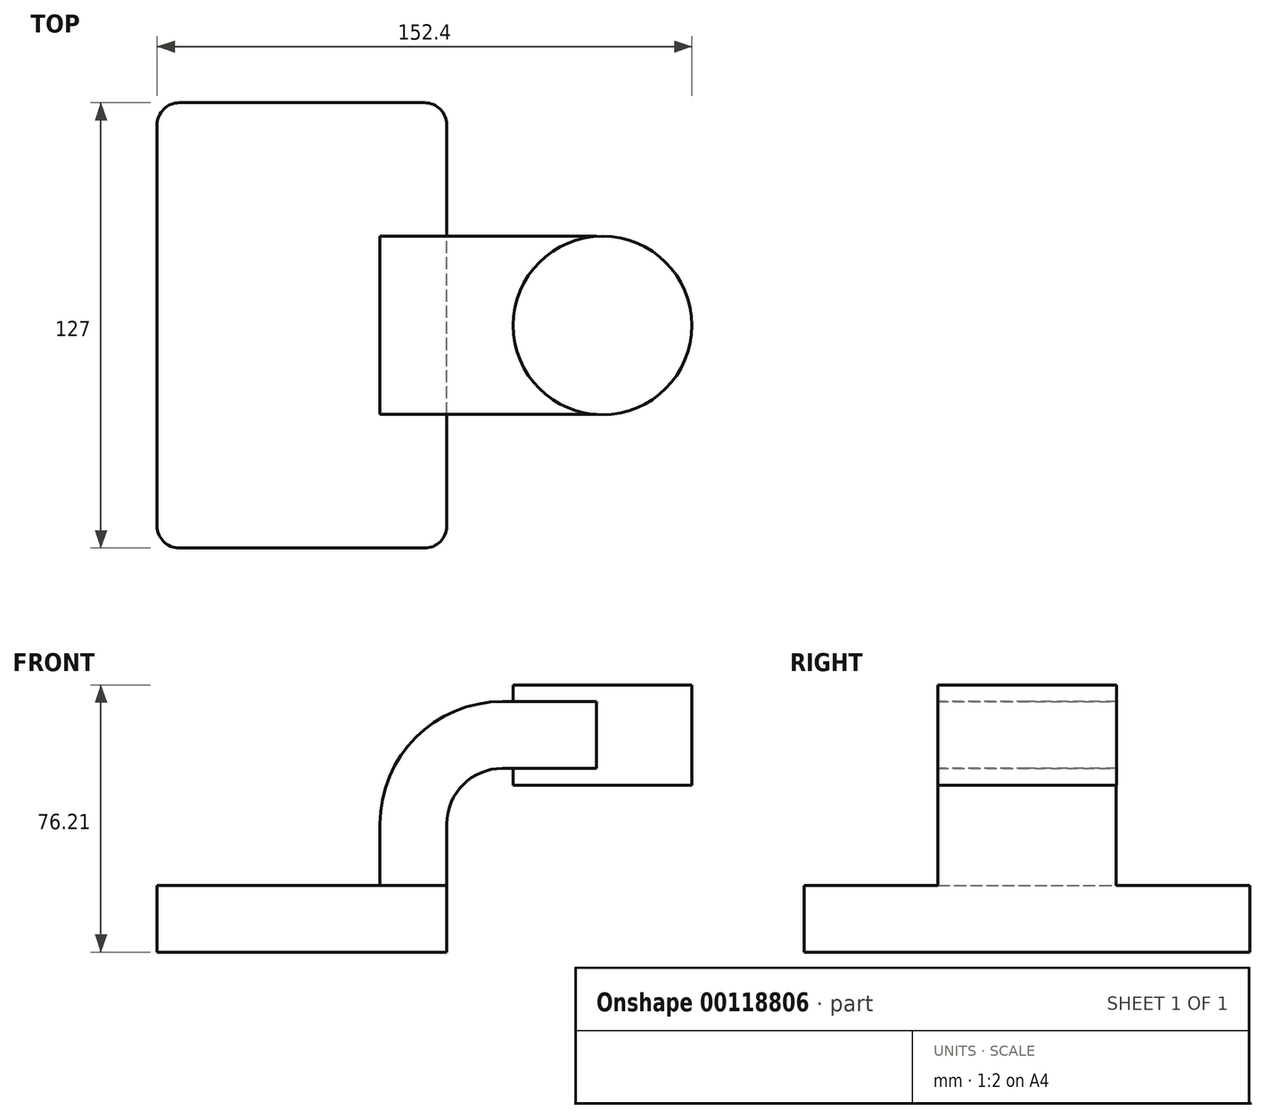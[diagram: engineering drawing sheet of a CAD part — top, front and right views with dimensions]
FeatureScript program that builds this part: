
annotation { "Feature Type Name" : "Feature", "Feature Type Description" : "" }
export const myFeature = defineFeature(function(context is Context, id is Id, definition is map)
    precondition{}
    {
        {
            var Q0;
            Q0=qCreatedBy(makeId("Front.planeOp"),FACE);
            var sketch = newSketch(context, id + "F0", { "sketchPlane" : qUnion([Q0])});
            skLineSegment(sketch, "E0.bottom", {"start": v(-41.28, -9.53) * mm, "end": v(41.28, -9.53) * mm});
            skLineSegment(sketch, "E0.top", {"start": v(-41.28, 9.53) * mm, "end": v(41.28, 9.53) * mm});
            skLineSegment(sketch, "E0.left", {"start": v(-41.28, -9.53) * mm, "end": v(-41.28, 9.53) * mm});
            skLineSegment(sketch, "E0.right", {"start": v(41.28, -9.53) * mm, "end": v(41.28, 9.53) * mm});
            skPoint(sketch, "E0.middle", {"position": v(0, 0) * mm});
            skLineSegment(sketch, "E1.bottom", {"start": v(60.32, 38.1) * mm, "end": v(111.12, 38.1) * mm});
            skLineSegment(sketch, "E1.top", {"start": v(60.32, 66.67) * mm, "end": v(111.12, 66.67) * mm});
            skLineSegment(sketch, "E1.left", {"start": v(60.32, 38.1) * mm, "end": v(60.32, 66.67) * mm});
            skLineSegment(sketch, "E1.right", {"start": v(111.12, 38.1) * mm, "end": v(111.12, 66.67) * mm});
            skPoint(sketch, "E1.middle", {"position": v(85.72, 52.39) * mm});
            skLineSegment(sketch, "E2", {"start": v(41.28, 9.53) * mm, "end": v(41.28, 27) * mm});
            skArc(sketch, "E3", {"start": v(41.27, 27) * mm, "mid": v(45.92, 38.23) * mm, "end": v(57.15, 42.88) * mm});
            skLineSegment(sketch, "E4", {"start": v(57.15, 42.88) * mm, "end": v(85.66, 42.88) * mm});
            skLineSegment(sketch, "E5.0", {"start": v(57.15, 61.93) * mm, "end": v(85.66, 61.93) * mm});
            skArc(sketch, "E5.1", {"start": v(22.22, 27) * mm, "mid": v(32.45, 51.7) * mm, "end": v(57.15, 61.93) * mm});
            skLineSegment(sketch, "E5.2", {"start": v(22.22, 9.53) * mm, "end": v(22.22, 27) * mm});
            skLineSegment(sketch, "E6", {"start": v(85.66, 38.1) * mm, "end": v(85.66, 66.67) * mm});
            skFitSpline(sketch, "E7", {"points": [v(-41.28, 9.53) * mm, v(57.15, 61.93) * mm], "startDerivative": vector(0.8, 87.71) * mm, "endDerivative": vector(119.82, -11.25) * mm});
            skSolve(sketch);
        }
        {
            var Q0;
            Q0=makeQuery(id+"F0.imprint","IMPRINT",FACE,{"disambiguationData":[TD([[makeQuery(id+"F0.imprint","IMPRINT",EDGE,{"derivedFrom":sQuery(id+"F0.wireOp",EDGE,"E0.bottom")}),1.0]])]});
            extrude(context, id + "F1", {"entities" : qUnion([Q0]), "depth" : 127 * mm, "symmetric" : true});
        }
        {
            var Q0;
            {var subQ1=sQuery(id+"F0.wireOp",EDGE,"E2");Q0=makeQuery(id+"F0.imprint","IMPRINT",FACE,{"disambiguationData":[TD([[makeQuery(id+"F0.imprint","IMPRINT",EDGE,{"derivedFrom":subQ1}),1.0]])]});}
            var Q1;
            {var subQ0=sQuery(id+"F0.wireOp",EDGE,"E4");var subQ1=sQuery(id+"F0.wireOp",EDGE,"E1.left");var subQ2=makeQuery(id+"F0.imprint","INTERSECT",VERTEX,{"derivedFrom":[subQ1,subQ0]});Q1=makeQuery(id+"F0.imprint","IMPRINT",FACE,{"disambiguationData":[TD([[makeQuery(id+"F0.imprint","IMPRINT",EDGE,{"disambiguationData":[TD([[subQ2,-1.0]])],"derivedFrom":subQ1}),-1.0]])]});}
            extrude(context, id + "F2", {"entities" : qUnion([Q0, Q1]), "operationType" : NewBodyOperationType.ADD, "depth" : 50.8 * mm, "symmetric" : true});
        }
        {
            var Q0;
            Q0=makeQuery(id+"F0.imprint","IMPRINT",FACE,{"disambiguationData":[TD([[makeQuery(id+"F0.imprint","IMPRINT",EDGE,{"derivedFrom":sQuery(id+"F0.wireOp",EDGE,"E5.1")}),1.0]])]});
            extrude(context, id + "F3", {"entities" : qUnion([Q0]), "operationType" : NewBodyOperationType.ADD, "depth" : 15.88 * mm, "symmetric" : true});
        }
        {
            var Q0;
            {var subQ0=sQuery(id+"F0.wireOp",EDGE,"E1.right");Q0=makeQuery(id+"F0.imprint","IMPRINT",FACE,{"disambiguationData":[TD([[makeQuery(id+"F0.imprint","IMPRINT",EDGE,{"derivedFrom":subQ0}),1.0]])]});}
            var Q1;
            Q1=sQuery(id+"F0.wireOp",EDGE,"E6");
            revolve(context, id + "F4", {"operationType" : NewBodyOperationType.ADD, "entities" : qUnion([Q0]), "axis" : qUnion([Q1]), "revolveType" : RevolveType.FULL});
        }
        {
            var Q0;
            Q0=makeQuery(id+"F1.opExtrude","CAP_EDGE",EDGE,{"disambiguationData":[OSD([sQuery(id+"F0.wireOp",EDGE,"E0.left")])],"isStart":false});
            var Q1;
            Q1=makeQuery(id+"F1.opExtrude","CAP_EDGE",EDGE,{"disambiguationData":[OSD([sQuery(id+"F0.wireOp",EDGE,"E0.right")])],"isStart":false});
            var Q2;
            Q2=makeQuery(id+"F1.opExtrude","CAP_EDGE",EDGE,{"disambiguationData":[OSD([sQuery(id+"F0.wireOp",EDGE,"E0.right")])],"isStart":true});
            var Q3;
            Q3=makeQuery(id+"F1.opExtrude","CAP_EDGE",EDGE,{"disambiguationData":[OSD([sQuery(id+"F0.wireOp",EDGE,"E0.left")])],"isStart":true});
            fillet(context, id + "F5", {"entities" : qUnion([Q0, Q1, Q2, Q3]), "radius" : 6.35 * mm, "tangentPropagation" : true, "allowEdgeOverflow" : false});
        }
    });
